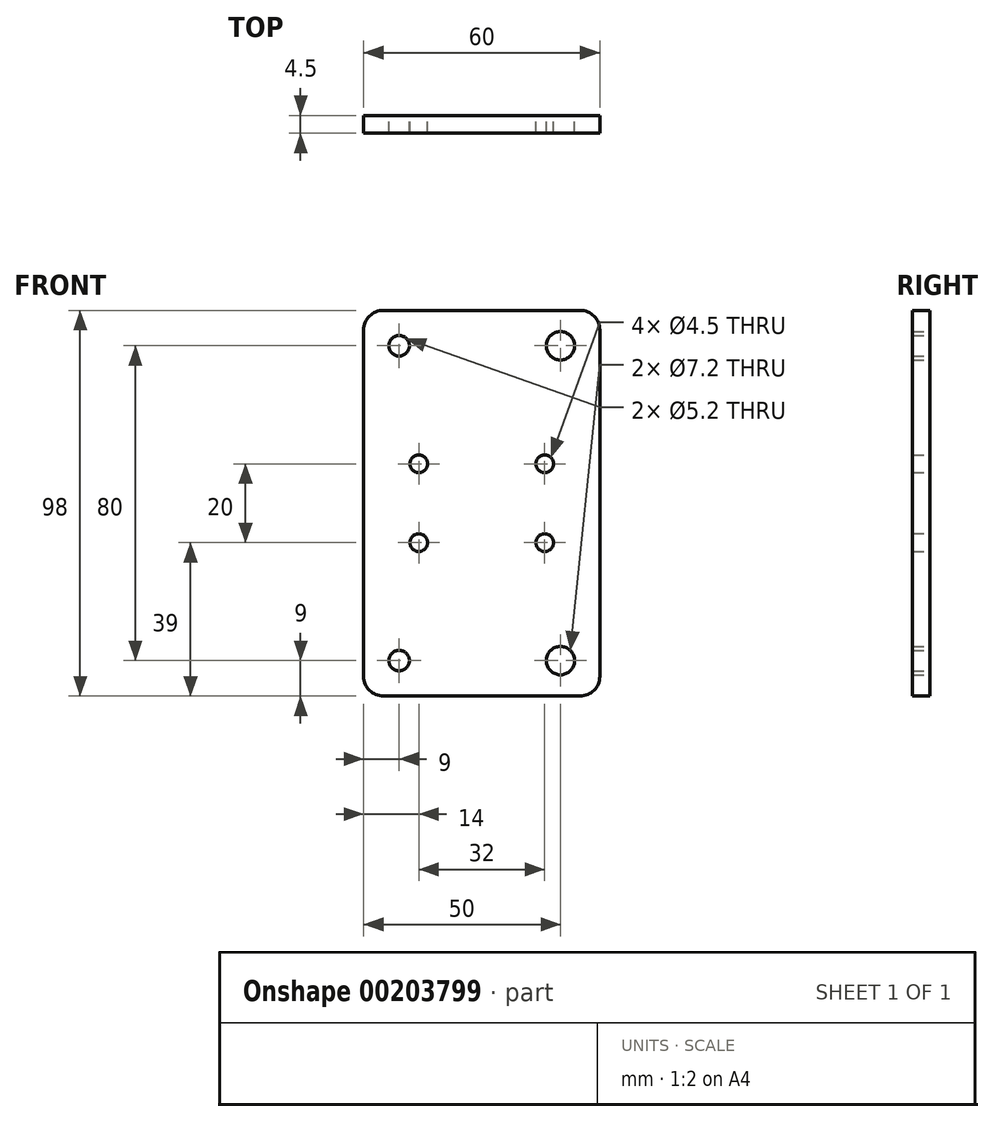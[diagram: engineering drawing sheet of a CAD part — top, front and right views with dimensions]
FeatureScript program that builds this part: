
annotation { "Feature Type Name" : "Feature", "Feature Type Description" : "" }
export const myFeature = defineFeature(function(context is Context, id is Id, definition is map)
    precondition{}
    {
        {
            var Q0;
            Q0=qCreatedBy(makeId("Front.planeOp"),FACE);
            var sketch = newSketch(context, id + "F0", { "sketchPlane" : qUnion([Q0])});
            skLineSegment(sketch, "E0.bottom", {"start": v(30, 49) * mm, "end": v(-30, 49) * mm});
            skLineSegment(sketch, "E0.top", {"start": v(30, -49) * mm, "end": v(-30, -49) * mm});
            skLineSegment(sketch, "E0.left", {"start": v(30, 49) * mm, "end": v(30, -49) * mm});
            skLineSegment(sketch, "E0.right", {"start": v(-30, 49) * mm, "end": v(-30, -49) * mm});
            skPoint(sketch, "E0.middle", {"position": v(0, 0) * mm});
            skLineSegment(sketch, "E1", {"start": v(0, 0) * mm, "end": v(0, 40) * mm, "construction": true});
            skLineSegment(sketch, "E2", {"start": v(0, 40) * mm, "end": v(-21, 40) * mm, "construction": true});
            skCircle(sketch, "E3", {"center": v(-21, 40) * mm, "radius": 2.6 * mm});
            skLineSegment(sketch, "E4", {"start": v(0, 40) * mm, "end": v(20, 40) * mm, "construction": true});
            skCircle(sketch, "E5", {"center": v(20, 40) * mm, "radius": 3.6 * mm});
            skLineSegment(sketch, "E6", {"start": v(0, 0) * mm, "end": v(0, 10) * mm, "construction": true});
            skLineSegment(sketch, "E7", {"start": v(0, 10) * mm, "end": v(-16, 10) * mm, "construction": true});
            skCircle(sketch, "E8", {"center": v(-16, 10) * mm, "radius": 2.25 * mm});
            skCircle(sketch, "E9.MirrorC", {"center": v(16, 10) * mm, "radius": 2.25 * mm});
            skCircle(sketch, "E10.MirrorC", {"center": v(-16, -10) * mm, "radius": 2.25 * mm});
            skCircle(sketch, "E11.MirrorC", {"center": v(16, -10) * mm, "radius": 2.25 * mm});
            skCircle(sketch, "E12.MirrorC", {"center": v(20, -40) * mm, "radius": 3.6 * mm});
            skCircle(sketch, "E13.MirrorC", {"center": v(-21, -40) * mm, "radius": 2.6 * mm});
            skLineSegment(sketch, "E14", {"start": v(20, 40) * mm, "end": v(20, -63.52) * mm, "construction": true});
            skLineSegment(sketch, "E15", {"start": v(-21, 40) * mm, "end": v(-21, -66.33) * mm, "construction": true});
            skSolve(sketch);
        }
        {
            var Q0;
            Q0=makeQuery(id+"F0.imprint","IMPRINT",FACE,{"disambiguationData":[TD([[makeQuery(id+"F0.imprint","IMPRINT",EDGE,{"derivedFrom":sQuery(id+"F0.wireOp",EDGE,"E0.bottom")}),1.0]])]});
            extrude(context, id + "F1", {"entities" : qUnion([Q0]), "depth" : 4.5 * mm, "symmetric" : true});
        }
        {
            var Q0;
            Q0=makeQuery(id+"F1.opExtrude","SWEPT_EDGE",EDGE,{"disambiguationData":[OSD([sQuery(id+"F0.wireOp",EDGE,"E0.bottom"),sQuery(id+"F0.wireOp",EDGE,"E0.right")])]});
            var Q1;
            Q1=makeQuery(id+"F1.opExtrude","SWEPT_EDGE",EDGE,{"disambiguationData":[OSD([sQuery(id+"F0.wireOp",EDGE,"E0.bottom"),sQuery(id+"F0.wireOp",EDGE,"E0.left")])]});
            var Q2;
            Q2=makeQuery(id+"F1.opExtrude","SWEPT_EDGE",EDGE,{"disambiguationData":[OSD([sQuery(id+"F0.wireOp",EDGE,"E0.top"),sQuery(id+"F0.wireOp",EDGE,"E0.left")])]});
            var Q3;
            Q3=makeQuery(id+"F1.opExtrude","SWEPT_EDGE",EDGE,{"disambiguationData":[OSD([sQuery(id+"F0.wireOp",EDGE,"E0.top"),sQuery(id+"F0.wireOp",EDGE,"E0.right")])]});
            fillet(context, id + "F2", {"entities" : qUnion([Q0, Q1, Q2, Q3]), "radius" : 5 * mm, "tangentPropagation" : true, "allowEdgeOverflow" : false});
        }
    });
